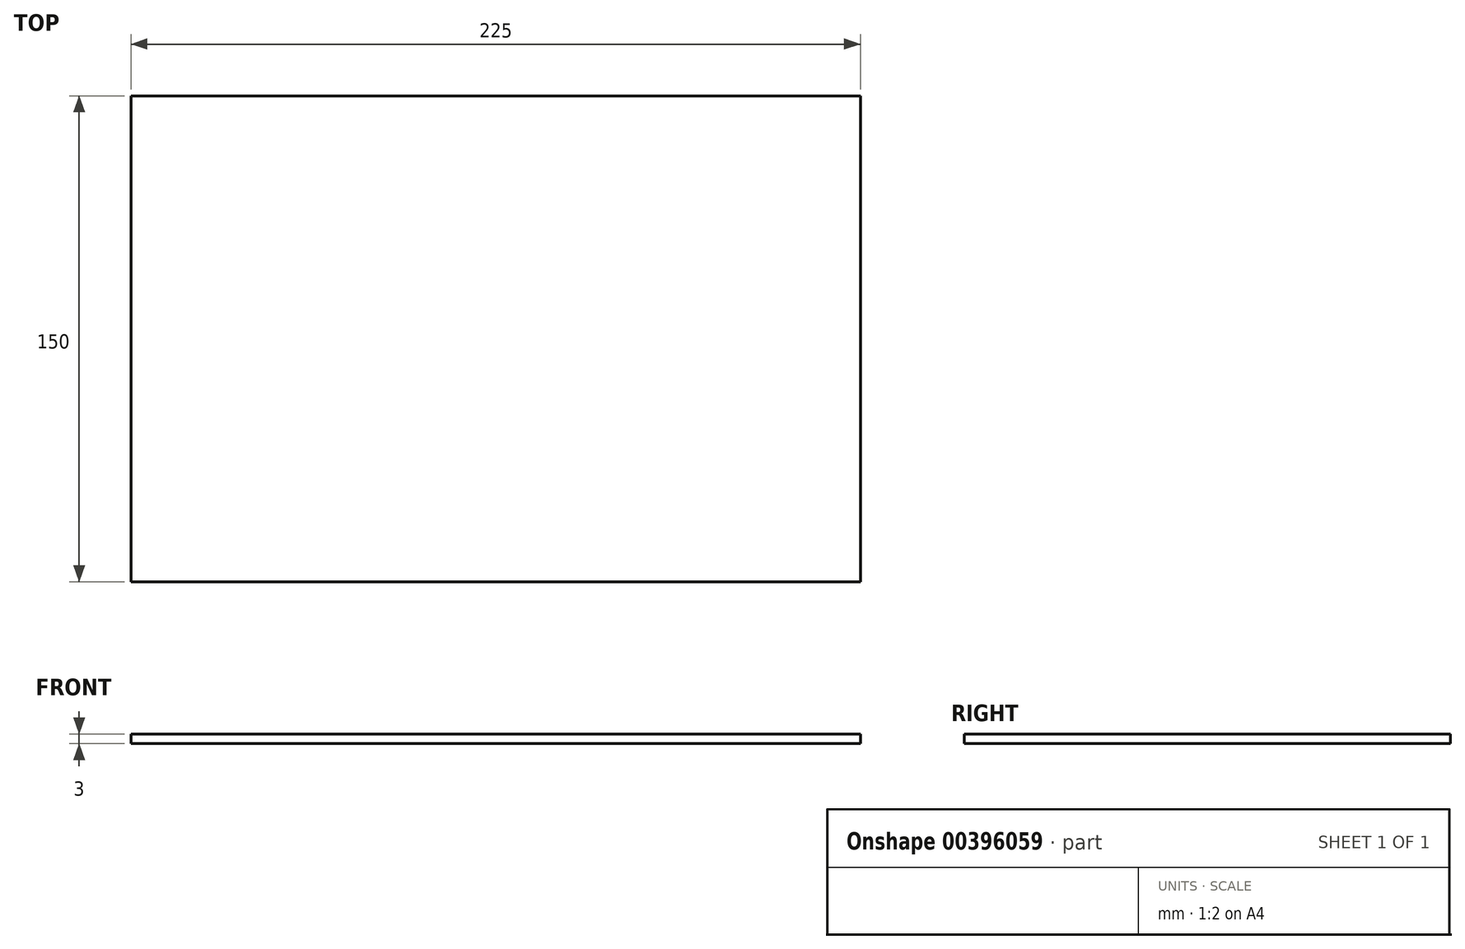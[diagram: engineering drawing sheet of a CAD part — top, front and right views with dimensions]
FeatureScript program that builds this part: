
annotation { "Feature Type Name" : "Feature", "Feature Type Description" : "" }
export const myFeature = defineFeature(function(context is Context, id is Id, definition is map)
    precondition{}
    {
        {
            var Q0;
            Q0=qCreatedBy(makeId("Top.planeOp"),FACE);
            var sketch = newSketch(context, id + "F0", { "sketchPlane" : qUnion([Q0])});
            skPoint(sketch, "E0.middle", {"position": v(0, 0) * mm});
            skLineSegment(sketch, "E1.bottom", {"start": v(-112.5, 75) * mm, "end": v(112.5, 75) * mm});
            skLineSegment(sketch, "E1.top", {"start": v(-112.5, -75) * mm, "end": v(112.5, -75) * mm});
            skLineSegment(sketch, "E1.left", {"start": v(-112.5, 75) * mm, "end": v(-112.5, -75) * mm});
            skLineSegment(sketch, "E1.right", {"start": v(112.5, 75) * mm, "end": v(112.5, -75) * mm});
            skSolve(sketch);
        }
        {
            var Q0;
            Q0=qSketchRegion(id+"F0",true);
            extrude(context, id + "F1", {"entities" : qUnion([Q0]), "depth" : 3 * mm});
        }
    });
